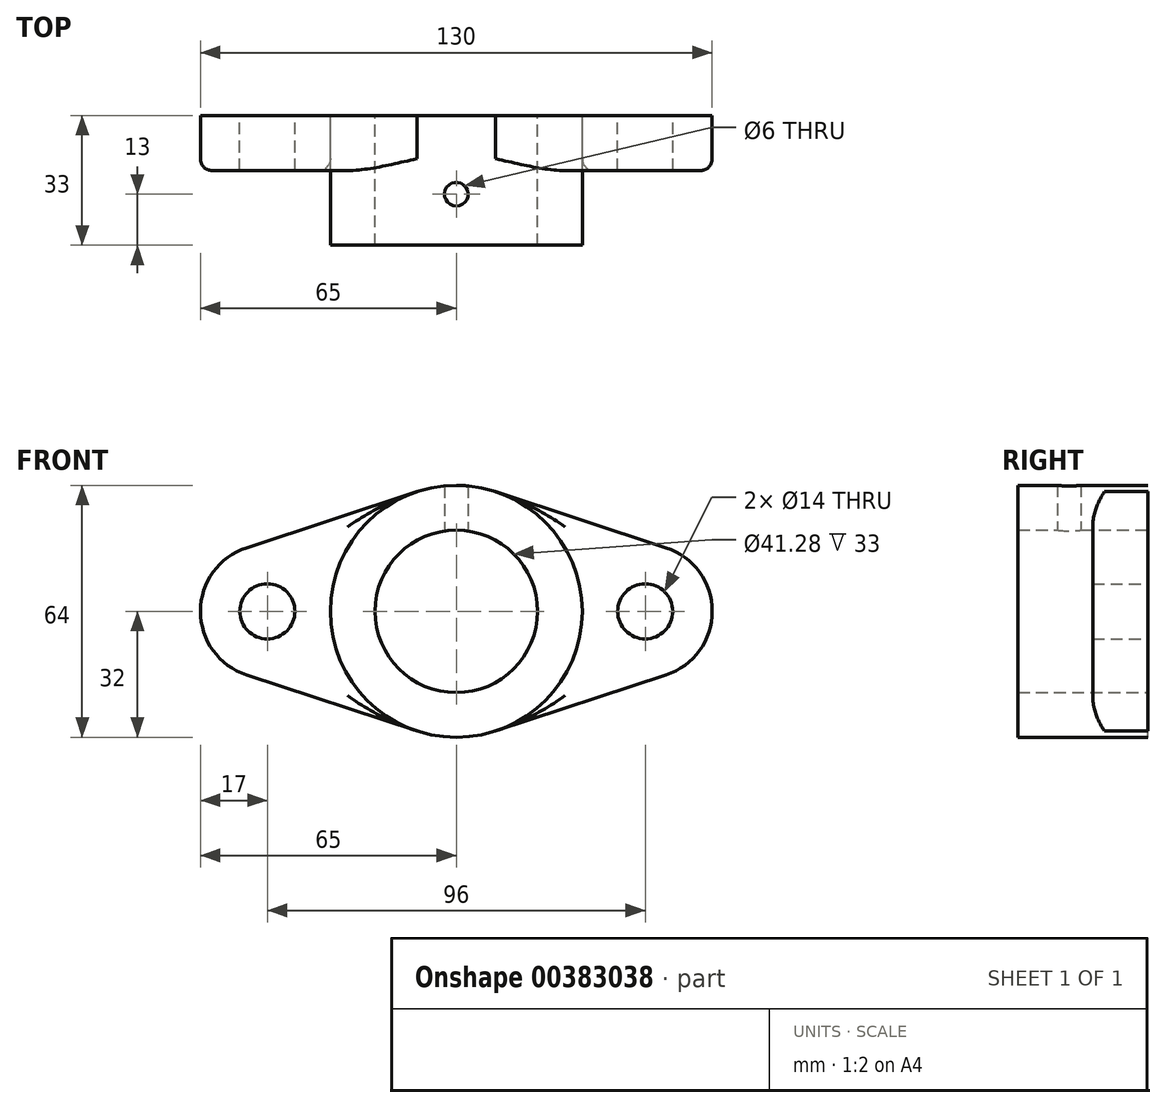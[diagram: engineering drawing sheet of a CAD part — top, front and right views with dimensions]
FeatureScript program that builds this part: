
annotation { "Feature Type Name" : "Feature", "Feature Type Description" : "" }
export const myFeature = defineFeature(function(context is Context, id is Id, definition is map)
    precondition{}
    {
        {
            var Q0;
            Q0=qCreatedBy(makeId("Front.planeOp"),FACE);
            var sketch = newSketch(context, id + "F0", { "sketchPlane" : qUnion([Q0])});
            skCircle(sketch, "E0", {"center": v(0, 0) * mm, "radius": 32 * mm});
            skCircle(sketch, "E1", {"center": v(-48, 0) * mm, "radius": 7 * mm});
            skCircle(sketch, "E2", {"center": v(48, 0) * mm, "radius": 7 * mm});
            skCircle(sketch, "E3", {"center": v(0, 0) * mm, "radius": 20.64 * mm});
            skArc(sketch, "E4", {"start": v(-53.31, 16.15) * mm, "mid": v(-65, 0) * mm, "end": v(-53.31, -16.15) * mm});
            skArc(sketch, "E5", {"start": v(53.31, -16.15) * mm, "mid": v(65, 0) * mm, "end": v(53.31, 16.15) * mm});
            skLineSegment(sketch, "E6", {"start": v(-53.31, 16.15) * mm, "end": v(-10, 30.4) * mm});
            skLineSegment(sketch, "E7", {"start": v(10, 30.4) * mm, "end": v(53.31, 16.15) * mm});
            skLineSegment(sketch, "E8", {"start": v(-53.31, -16.15) * mm, "end": v(-10, -30.4) * mm});
            skLineSegment(sketch, "E9", {"start": v(10, -30.4) * mm, "end": v(53.31, -16.15) * mm});
            skSolve(sketch);
        }
        {
            var Q0;
            Q0=makeQuery(id+"F0.imprint","IMPRINT",FACE,{"disambiguationData":[TD([[makeQuery(id+"F0.imprint","IMPRINT",EDGE,{"derivedFrom":sQuery(id+"F0.wireOp",EDGE,"E1")}),-1.0]])]});
            var Q1;
            Q1=makeQuery(id+"F0.imprint","IMPRINT",FACE,{"disambiguationData":[TD([[makeQuery(id+"F0.imprint","IMPRINT",EDGE,{"derivedFrom":sQuery(id+"F0.wireOp",EDGE,"E2")}),-1.0]])]});
            extrude(context, id + "F1", {"entities" : qUnion([Q0, Q1]), "depth" : 14 * mm});
        }
        {
            var Q0;
            Q0=makeQuery(id+"F0.imprint","IMPRINT",FACE,{"disambiguationData":[TD([[makeQuery(id+"F0.imprint","IMPRINT",EDGE,{"derivedFrom":sQuery(id+"F0.wireOp",EDGE,"E3")}),-1.0]])]});
            extrude(context, id + "F2", {"entities" : qUnion([Q0]), "depth" : 33 * mm});
        }
        {
            var Q0;
            Q0=qCreatedBy(makeId("Top.planeOp"),FACE);
            var sketch = newSketch(context, id + "F3", { "sketchPlane" : qUnion([Q0])});
            skCircle(sketch, "E10", {"center": v(0, -20) * mm, "radius": 3 * mm});
            skSolve(sketch);
        }
        {
            var Q0;
            Q0=makeQuery(id+"F3.imprint","IMPRINT",FACE,{"disambiguationData":[TD([[makeQuery(id+"F3.imprint","IMPRINT",EDGE,{"derivedFrom":sQuery(id+"F3.wireOp",EDGE,"E10")}),1.0]])]});
            extrude(context, id + "F4", {"entities" : qUnion([Q0]), "operationType" : NewBodyOperationType.REMOVE, "endBound" : BoundingType.THROUGH_ALL, "depth" : 25 * mm});
        }
        {
            var Q0;
            {var subQ0=sQuery(id+"F0.wireOp",EDGE,"E0");Q0=makeQuery(id+"F1.opExtrude","CAP_EDGE",EDGE,{"disambiguationData":[OSD([subQ0]),TDD([makeQuery(id+"F0.imprint","IMPRINT",EDGE,{"disambiguationData":[TD([[makeQuery(id+"F0.imprint","INTERSECT",VERTEX,{"derivedFrom":[subQ0,sQuery(id+"F0.wireOp",EDGE,"E7")]}),1.0]])],"derivedFrom":subQ0})])],"isStart":false});}
            var Q1;
            Q1=makeQuery(id+"F1.opExtrude","CAP_EDGE",EDGE,{"disambiguationData":[OSD([sQuery(id+"F0.wireOp",EDGE,"E7")])],"isStart":false});
            var Q2;
            {var subQ0=sQuery(id+"F0.wireOp",EDGE,"E0");Q2=makeQuery(id+"F1.opExtrude","CAP_EDGE",EDGE,{"disambiguationData":[OSD([subQ0]),TDD([makeQuery(id+"F0.imprint","IMPRINT",EDGE,{"disambiguationData":[TD([[makeQuery(id+"F0.imprint","INTERSECT",VERTEX,{"derivedFrom":[subQ0,sQuery(id+"F0.wireOp",EDGE,"E6")]}),-1.0]])],"derivedFrom":subQ0})])],"isStart":false});}
            var Q3;
            Q3=makeQuery(id+"F1.opExtrude","CAP_EDGE",EDGE,{"disambiguationData":[OSD([sQuery(id+"F0.wireOp",EDGE,"E6")])],"isStart":false});
            fillet(context, id + "F5", {"entities" : qUnion([Q0, Q1, Q2, Q3]), "radius" : 3 * mm, "tangentPropagation" : true, "allowEdgeOverflow" : false});
        }
    });
